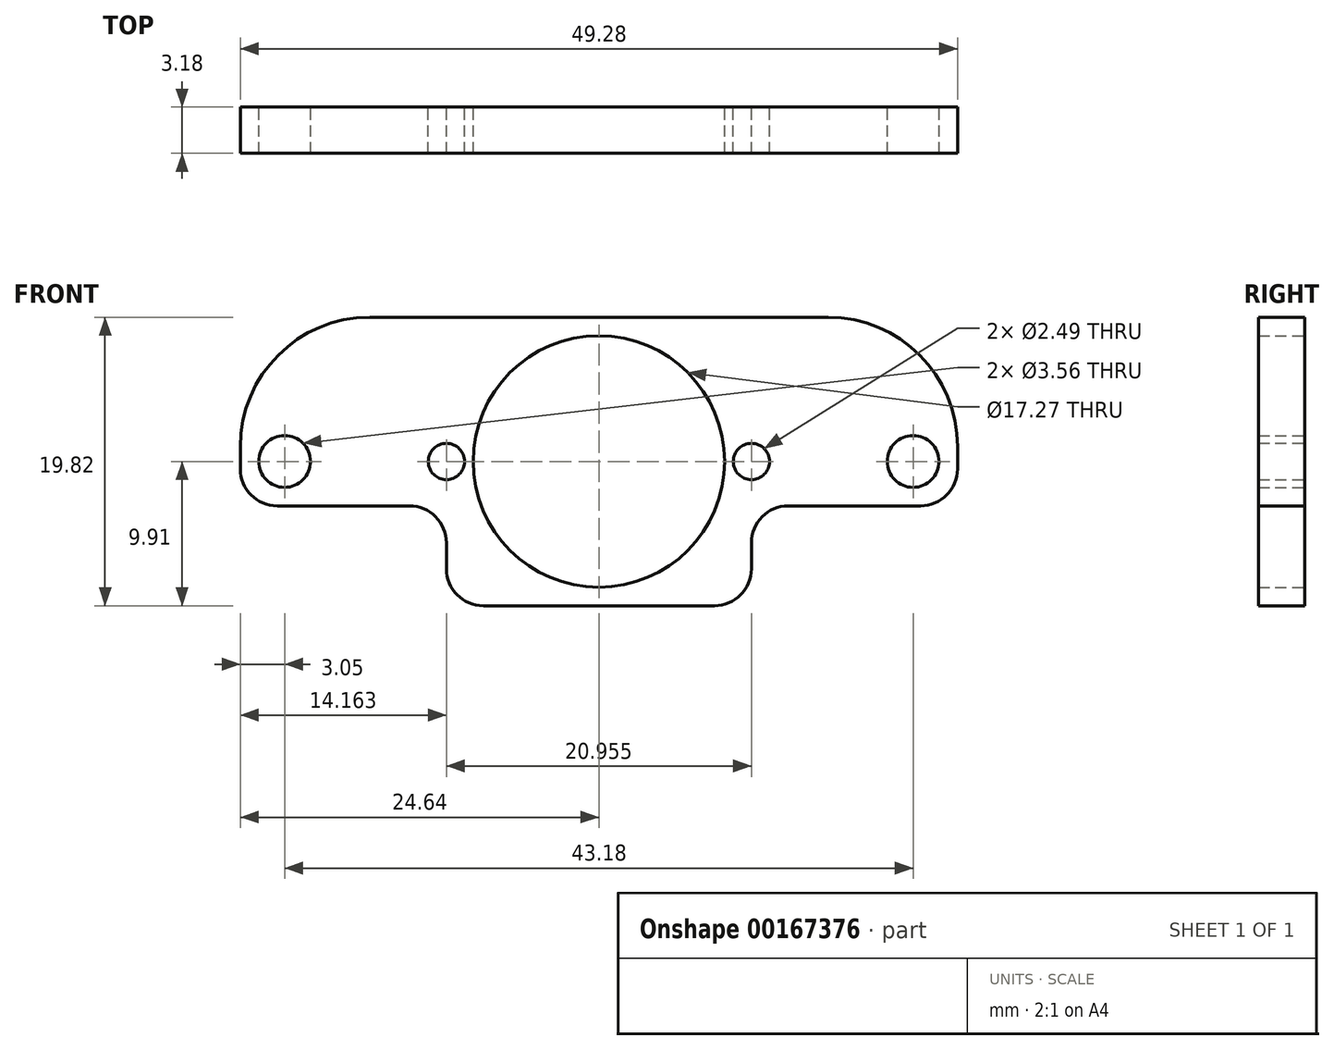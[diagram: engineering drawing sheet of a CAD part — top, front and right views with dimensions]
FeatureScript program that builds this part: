
annotation { "Feature Type Name" : "Feature", "Feature Type Description" : "" }
export const myFeature = defineFeature(function(context is Context, id is Id, definition is map)
    precondition{}
    {
        {
            var Q0;
            Q0=qCreatedBy(makeId("Front.planeOp"),FACE);
            var sketch = newSketch(context, id + "F0", { "sketchPlane" : qUnion([Q0])});
            skPoint(sketch, "E0.middle", {"position": v(0, 0) * mm});
            skCircle(sketch, "E1", {"center": v(0, 0) * mm, "radius": 8.64 * mm});
            skCircle(sketch, "E2", {"center": v(-10.48, 0) * mm, "radius": 1.24 * mm});
            skCircle(sketch, "E3", {"center": v(10.48, 0) * mm, "radius": 1.24 * mm});
            skCircle(sketch, "E4", {"center": v(-21.59, 0) * mm, "radius": 1.78 * mm});
            skCircle(sketch, "E5", {"center": v(21.59, 0) * mm, "radius": 1.78 * mm});
            skLineSegment(sketch, "E6.bottom", {"start": v(24.64, 9.9) * mm, "end": v(-24.64, 9.9) * mm});
            skLineSegment(sketch, "E6.top", {"start": v(10.48, -9.9) * mm, "end": v(-10.48, -9.9) * mm});
            skLineSegment(sketch, "E6.left", {"start": v(24.64, 9.9) * mm, "end": v(24.64, -3.05) * mm});
            skLineSegment(sketch, "E6.right", {"start": v(-24.64, 9.9) * mm, "end": v(-24.64, -3.05) * mm});
            skLineSegment(sketch, "E7", {"start": v(-24.64, -3.05) * mm, "end": v(-10.48, -3.05) * mm});
            skLineSegment(sketch, "E8", {"start": v(-10.48, -3.05) * mm, "end": v(-10.48, -9.9) * mm});
            skLineSegment(sketch, "E9", {"start": v(24.64, -3.05) * mm, "end": v(10.48, -3.05) * mm});
            skLineSegment(sketch, "E10", {"start": v(10.48, -3.05) * mm, "end": v(10.48, -9.9) * mm});
            skSolve(sketch);
        }
        {
            var Q0;
            Q0=makeQuery(id+"F0.imprint","IMPRINT",FACE,{"disambiguationData":[TD([[makeQuery(id+"F0.imprint","IMPRINT",EDGE,{"derivedFrom":sQuery(id+"F0.wireOp",EDGE,"E1")}),-1.0]])]});
            extrude(context, id + "F1", {"entities" : qUnion([Q0]), "depth" : 3.17 * mm});
        }
        {
            var Q0;
            Q0=makeQuery(id+"F1.opExtrude","SWEPT_EDGE",EDGE,{"disambiguationData":[OSD([sQuery(id+"F0.wireOp",EDGE,"E6.bottom"),sQuery(id+"F0.wireOp",EDGE,"E6.right")])]});
            var Q1;
            Q1=makeQuery(id+"F1.opExtrude","SWEPT_EDGE",EDGE,{"disambiguationData":[OSD([sQuery(id+"F0.wireOp",EDGE,"E6.bottom"),sQuery(id+"F0.wireOp",EDGE,"E6.left")])]});
            fillet(context, id + "F2", {"entities" : qUnion([Q0, Q1]), "radius" : 8.9 * mm, "tangentPropagation" : true, "allowEdgeOverflow" : false});
        }
        {
            var Q0;
            Q0=makeQuery(id+"F1.opExtrude","SWEPT_EDGE",EDGE,{"disambiguationData":[OSD([sQuery(id+"F0.wireOp",EDGE,"E6.right"),sQuery(id+"F0.wireOp",EDGE,"E7")])]});
            var Q1;
            Q1=makeQuery(id+"F1.opExtrude","SWEPT_EDGE",EDGE,{"disambiguationData":[OSD([sQuery(id+"F0.wireOp",EDGE,"E7"),sQuery(id+"F0.wireOp",EDGE,"E8")])]});
            var Q2;
            Q2=makeQuery(id+"F1.opExtrude","SWEPT_EDGE",EDGE,{"disambiguationData":[OSD([sQuery(id+"F0.wireOp",EDGE,"E6.top"),sQuery(id+"F0.wireOp",EDGE,"E8")])]});
            var Q3;
            Q3=makeQuery(id+"F1.opExtrude","SWEPT_EDGE",EDGE,{"disambiguationData":[OSD([sQuery(id+"F0.wireOp",EDGE,"E6.top"),sQuery(id+"F0.wireOp",EDGE,"E10")])]});
            var Q4;
            Q4=makeQuery(id+"F1.opExtrude","SWEPT_EDGE",EDGE,{"disambiguationData":[OSD([sQuery(id+"F0.wireOp",EDGE,"E6.left"),sQuery(id+"F0.wireOp",EDGE,"E9")])]});
            var Q5;
            Q5=makeQuery(id+"F1.opExtrude","SWEPT_EDGE",EDGE,{"disambiguationData":[OSD([sQuery(id+"F0.wireOp",EDGE,"E9"),sQuery(id+"F0.wireOp",EDGE,"E10")])]});
            fillet(context, id + "F3", {"entities" : qUnion([Q0, Q1, Q2, Q3, Q4, Q5]), "radius" : 2.54 * mm, "tangentPropagation" : true, "allowEdgeOverflow" : false});
        }
    });
